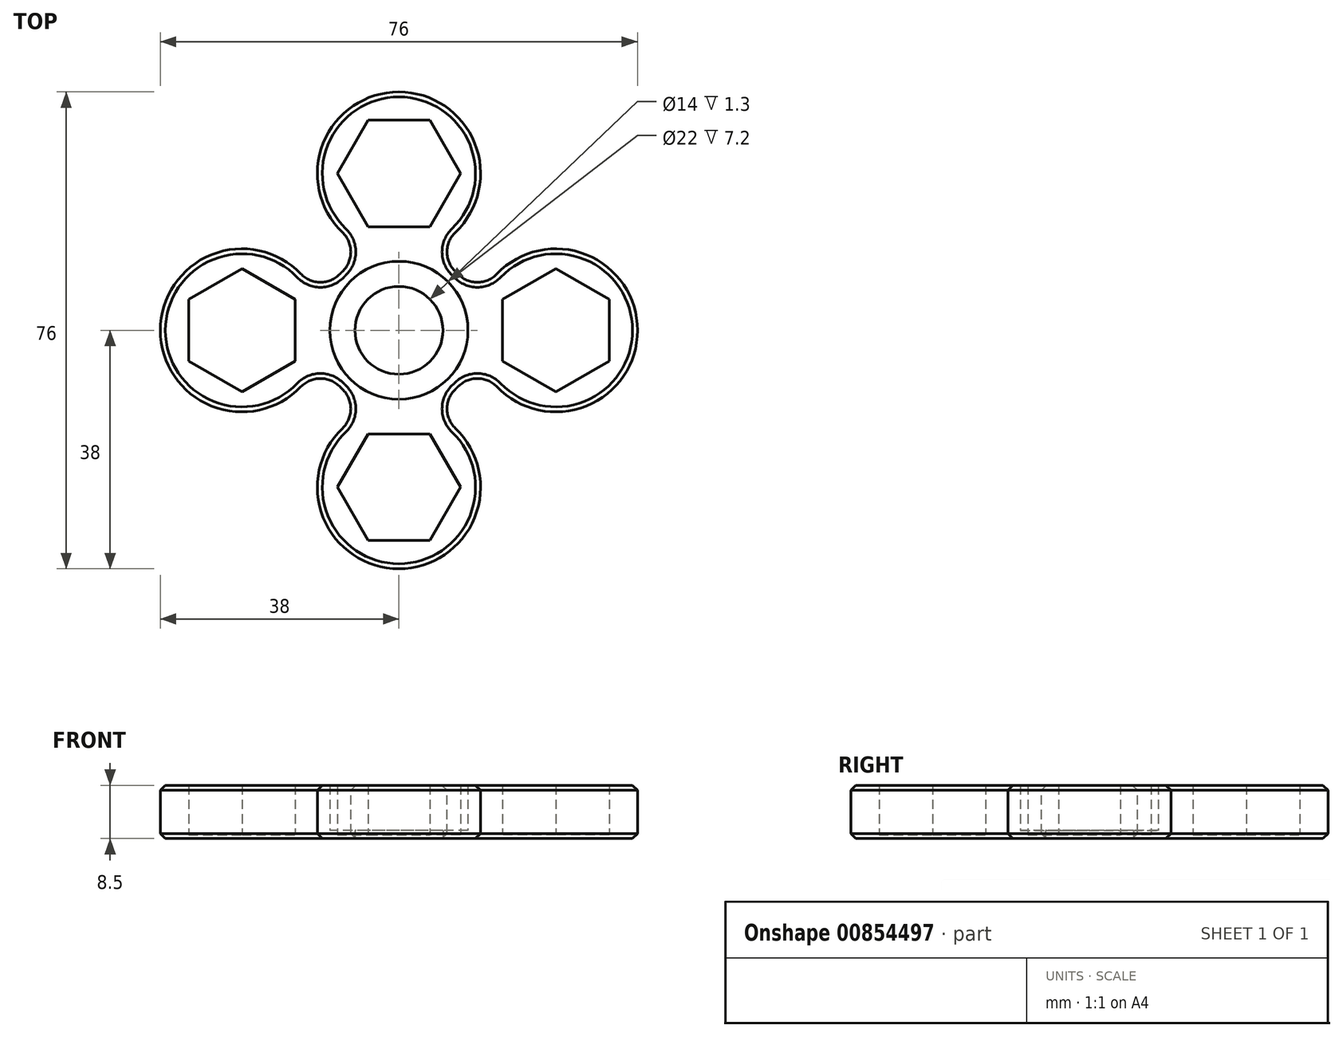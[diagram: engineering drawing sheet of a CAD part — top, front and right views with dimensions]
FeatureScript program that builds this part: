
annotation { "Feature Type Name" : "Feature", "Feature Type Description" : "" }
export const myFeature = defineFeature(function(context is Context, id is Id, definition is map)
    precondition{}
    {
        {
            var Q0;
            Q0=qCreatedBy(makeId("Top.planeOp"),FACE);
            var sketch = newSketch(context, id + "F0", { "sketchPlane" : qUnion([Q0])});
            skCircle(sketch, "E0", {"center": v(0, 0) * mm, "radius": 13 * mm});
            skCircle(sketch, "E1", {"center": v(0, 0) * mm, "radius": 11 * mm});
            skCircle(sketch, "E2", {"center": v(0, 25) * mm, "radius": 13 * mm});
            skCircle(sketch, "E3.cCircle", {"center": v(0, 25) * mm, "radius": 8.5 * mm, "construction": true});
            skLineSegment(sketch, "E3.0", {"start": v(9.81, 25) * mm, "end": v(4.9, 16.5) * mm});
            skLineSegment(sketch, "E3.1", {"start": v(4.9, 16.5) * mm, "end": v(-4.9, 16.5) * mm});
            skLineSegment(sketch, "E3.2", {"start": v(-4.9, 16.5) * mm, "end": v(-9.81, 25) * mm});
            skLineSegment(sketch, "E3.3", {"start": v(-9.81, 25) * mm, "end": v(-4.9, 33.5) * mm});
            skLineSegment(sketch, "E3.4", {"start": v(-4.9, 33.5) * mm, "end": v(4.9, 33.5) * mm});
            skLineSegment(sketch, "E3.5", {"start": v(4.9, 33.5) * mm, "end": v(9.81, 25) * mm});
            skPoint(sketch, "E3.0.midPoint", {"position": v(7.36, 20.75) * mm});
            skCircle(sketch, "E4", {"center": v(0, 0) * mm, "radius": 7 * mm});
            skCircle(sketch, "E5.1.0", {"center": v(-25, 0) * mm, "radius": 13 * mm});
            skLineSegment(sketch, "E5.1.1", {"start": v(-16.5, -4.9) * mm, "end": v(-25, -9.81) * mm});
            skLineSegment(sketch, "E5.1.2", {"start": v(-25, -9.81) * mm, "end": v(-33.5, -4.9) * mm});
            skLineSegment(sketch, "E5.1.3", {"start": v(-33.5, -4.9) * mm, "end": v(-33.5, 4.9) * mm});
            skLineSegment(sketch, "E5.1.4", {"start": v(-33.5, 4.9) * mm, "end": v(-25, 9.81) * mm});
            skLineSegment(sketch, "E5.1.5", {"start": v(-25, 9.81) * mm, "end": v(-16.5, 4.9) * mm});
            skLineSegment(sketch, "E5.1.6", {"start": v(-16.5, 4.9) * mm, "end": v(-16.5, -4.9) * mm});
            skCircle(sketch, "E5.2.0", {"center": v(0, -25) * mm, "radius": 13 * mm});
            skLineSegment(sketch, "E5.2.1", {"start": v(4.9, -16.5) * mm, "end": v(9.81, -25) * mm});
            skLineSegment(sketch, "E5.2.2", {"start": v(9.81, -25) * mm, "end": v(4.9, -33.5) * mm});
            skLineSegment(sketch, "E5.2.3", {"start": v(4.9, -33.5) * mm, "end": v(-4.9, -33.5) * mm});
            skLineSegment(sketch, "E5.2.4", {"start": v(-4.9, -33.5) * mm, "end": v(-9.81, -25) * mm});
            skLineSegment(sketch, "E5.2.5", {"start": v(-9.81, -25) * mm, "end": v(-4.9, -16.5) * mm});
            skLineSegment(sketch, "E5.2.6", {"start": v(-4.9, -16.5) * mm, "end": v(4.9, -16.5) * mm});
            skCircle(sketch, "E5.3.0", {"center": v(25, 0) * mm, "radius": 13 * mm});
            skLineSegment(sketch, "E5.3.1", {"start": v(16.5, 4.9) * mm, "end": v(25, 9.81) * mm});
            skLineSegment(sketch, "E5.3.2", {"start": v(25, 9.81) * mm, "end": v(33.5, 4.9) * mm});
            skLineSegment(sketch, "E5.3.3", {"start": v(33.5, 4.9) * mm, "end": v(33.5, -4.9) * mm});
            skLineSegment(sketch, "E5.3.4", {"start": v(33.5, -4.9) * mm, "end": v(25, -9.81) * mm});
            skLineSegment(sketch, "E5.3.5", {"start": v(25, -9.81) * mm, "end": v(16.5, -4.9) * mm});
            skLineSegment(sketch, "E5.3.6", {"start": v(16.5, -4.9) * mm, "end": v(16.5, 4.9) * mm});
            skSolve(sketch);
        }
        {
            var Q0;
            Q0=makeQuery(id+"F0.imprint","IMPRINT",FACE,{"disambiguationData":[TD([[makeQuery(id+"F0.imprint","IMPRINT",EDGE,{"derivedFrom":sQuery(id+"F0.wireOp",EDGE,"E3.0")}),1.0]])]});
            var Q1;
            Q1=makeQuery(id+"F0.imprint","IMPRINT",FACE,{"disambiguationData":[TD([[makeQuery(id+"F0.imprint","IMPRINT",EDGE,{"derivedFrom":sQuery(id+"F0.wireOp",EDGE,"E3.0")}),-1.0]])]});
            var Q2;
            Q2=makeQuery(id+"F0.imprint","IMPRINT",FACE,{"disambiguationData":[TD([[makeQuery(id+"F0.imprint","IMPRINT",EDGE,{"derivedFrom":sQuery(id+"F0.wireOp",EDGE,"E1")}),1.0]])]});
            var Q3;
            Q3=makeQuery(id+"F0.imprint","IMPRINT",FACE,{"disambiguationData":[TD([[makeQuery(id+"F0.imprint","IMPRINT",EDGE,{"derivedFrom":sQuery(id+"F0.wireOp",EDGE,"E1")}),-1.0]])]});
            var Q4;
            {var subQ0=sQuery(id+"F0.wireOp",EDGE,"E2");var subQ1=sQuery(id+"F0.wireOp",EDGE,"E0");var subQ2=makeQuery(id+"F0.imprint","INTERSECT",VERTEX,{"disambiguationData":[OD(0.0)],"derivedFrom":[subQ1,subQ0]});Q4=makeQuery(id+"F0.imprint","IMPRINT",FACE,{"disambiguationData":[TD([[makeQuery(id+"F0.imprint","IMPRINT",EDGE,{"disambiguationData":[TD([[subQ2,1.0]])],"derivedFrom":subQ1}),1.0]])]});}
            var Q5;
            {var subQ0=sQuery(id+"F0.wireOp",EDGE,"d04d9439-d31e-4a44-955d-4c44843ed1f90.MirrorC");var subQ1=sQuery(id+"F0.wireOp",EDGE,"E0");var subQ2=makeQuery(id+"F0.imprint","INTERSECT",VERTEX,{"disambiguationData":[OD(0.0)],"derivedFrom":[subQ1,subQ0]});Q5=makeQuery(id+"F0.imprint","IMPRINT",FACE,{"disambiguationData":[TD([[makeQuery(id+"F0.imprint","IMPRINT",EDGE,{"disambiguationData":[TD([[subQ2,-1.0]])],"derivedFrom":subQ1}),1.0]])]});}
            var Q6;
            Q6=makeQuery(id+"F0.imprint","IMPRINT",FACE,{"disambiguationData":[TD([[makeQuery(id+"F0.imprint","IMPRINT",EDGE,{"derivedFrom":sQuery(id+"F0.wireOp",EDGE,"235c1c98-600d-46e9-b86c-8ce5ef518ee80.MirrorCS")}),-1.0]])]});
            var Q7;
            Q7=makeQuery(id+"F0.imprint","IMPRINT",FACE,{"disambiguationData":[TD([[makeQuery(id+"F0.imprint","IMPRINT",EDGE,{"derivedFrom":sQuery(id+"F0.wireOp",EDGE,"235c1c98-600d-46e9-b86c-8ce5ef518ee80.MirrorCS")}),1.0]])]});
            var Q8;
            Q8=makeQuery(id+"F0.imprint","IMPRINT",FACE,{"disambiguationData":[TD([[makeQuery(id+"F0.imprint","IMPRINT",EDGE,{"derivedFrom":sQuery(id+"F0.wireOp",EDGE,"E5.1.1")}),1.0]])]});
            var Q9;
            Q9=makeQuery(id+"F0.imprint","IMPRINT",FACE,{"disambiguationData":[TD([[makeQuery(id+"F0.imprint","IMPRINT",EDGE,{"derivedFrom":sQuery(id+"F0.wireOp",EDGE,"E5.1.1")}),-1.0]])]});
            var Q10;
            Q10=makeQuery(id+"F0.imprint","IMPRINT",FACE,{"disambiguationData":[TD([[makeQuery(id+"F0.imprint","IMPRINT",EDGE,{"derivedFrom":sQuery(id+"F0.wireOp",EDGE,"E5.3.1")}),-1.0]])]});
            var Q11;
            Q11=makeQuery(id+"F0.imprint","IMPRINT",FACE,{"disambiguationData":[TD([[makeQuery(id+"F0.imprint","IMPRINT",EDGE,{"derivedFrom":sQuery(id+"F0.wireOp",EDGE,"E5.3.1")}),1.0]])]});
            var Q12;
            Q12=makeQuery(id+"F0.imprint","IMPRINT",FACE,{"disambiguationData":[TD([[makeQuery(id+"F0.imprint","IMPRINT",EDGE,{"derivedFrom":sQuery(id+"F0.wireOp",EDGE,"E5.2.1")}),1.0]])]});
            var Q13;
            Q13=makeQuery(id+"F0.imprint","IMPRINT",FACE,{"disambiguationData":[TD([[makeQuery(id+"F0.imprint","IMPRINT",EDGE,{"derivedFrom":sQuery(id+"F0.wireOp",EDGE,"E5.2.1")}),-1.0]])]});
            var Q14;
            {var subQ0=sQuery(id+"F0.wireOp",EDGE,"E5.2.0");var subQ1=sQuery(id+"F0.wireOp",EDGE,"E0");var subQ2=makeQuery(id+"F0.imprint","INTERSECT",VERTEX,{"disambiguationData":[OD(0.0)],"derivedFrom":[subQ1,subQ0]});Q14=makeQuery(id+"F0.imprint","IMPRINT",FACE,{"disambiguationData":[TD([[makeQuery(id+"F0.imprint","IMPRINT",EDGE,{"disambiguationData":[TD([[subQ2,-1.0]])],"derivedFrom":subQ1}),1.0]])]});}
            var Q15;
            {var subQ0=sQuery(id+"F0.wireOp",EDGE,"E5.3.0");var subQ1=sQuery(id+"F0.wireOp",EDGE,"E0");var subQ2=makeQuery(id+"F0.imprint","INTERSECT",VERTEX,{"disambiguationData":[OD(0.0)],"derivedFrom":[subQ1,subQ0]});Q15=makeQuery(id+"F0.imprint","IMPRINT",FACE,{"disambiguationData":[TD([[makeQuery(id+"F0.imprint","IMPRINT",EDGE,{"disambiguationData":[TD([[subQ2,1.0]])],"derivedFrom":subQ1}),1.0]])]});}
            var Q16;
            {var subQ0=sQuery(id+"F0.wireOp",EDGE,"E5.1.0");var subQ1=sQuery(id+"F0.wireOp",EDGE,"E0");var subQ2=makeQuery(id+"F0.imprint","INTERSECT",VERTEX,{"disambiguationData":[OD(0.0)],"derivedFrom":[subQ1,subQ0]});Q16=makeQuery(id+"F0.imprint","IMPRINT",FACE,{"disambiguationData":[TD([[makeQuery(id+"F0.imprint","IMPRINT",EDGE,{"disambiguationData":[TD([[subQ2,-1.0]])],"derivedFrom":subQ1}),1.0]])]});}
            var Q17;
            {var subQ0=sQuery(id+"F0.wireOp",EDGE,"E2");var subQ1=sQuery(id+"F0.wireOp",EDGE,"E0");var subQ2=makeQuery(id+"F0.imprint","INTERSECT",VERTEX,{"disambiguationData":[OD(0.0)],"derivedFrom":[subQ1,subQ0]});Q17=makeQuery(id+"F0.imprint","IMPRINT",FACE,{"disambiguationData":[TD([[makeQuery(id+"F0.imprint","IMPRINT",EDGE,{"disambiguationData":[TD([[subQ2,-1.0]])],"derivedFrom":subQ1}),1.0]])]});}
            extrude(context, id + "F1", {"entities" : qUnion([Q0, Q1, Q2, Q3, Q4, Q5, Q6, Q7, Q8, Q9, Q10, Q11, Q12, Q13, Q14, Q15, Q16, Q17]), "depth" : 0.6 * mm, "offsetDistance" : 25 * mm});
        }
        {
            var Q0;
            Q0=makeQuery(id+"F0.imprint","IMPRINT",FACE,{"disambiguationData":[TD([[makeQuery(id+"F0.imprint","IMPRINT",EDGE,{"derivedFrom":sQuery(id+"F0.wireOp",EDGE,"E5.3.1")}),1.0]])]});
            var Q1;
            Q1=makeQuery(id+"F0.imprint","IMPRINT",FACE,{"disambiguationData":[TD([[makeQuery(id+"F0.imprint","IMPRINT",EDGE,{"derivedFrom":sQuery(id+"F0.wireOp",EDGE,"E1")}),-1.0]])]});
            var Q2;
            Q2=makeQuery(id+"F0.imprint","IMPRINT",FACE,{"disambiguationData":[TD([[makeQuery(id+"F0.imprint","IMPRINT",EDGE,{"derivedFrom":sQuery(id+"F0.wireOp",EDGE,"E5.2.1")}),1.0]])]});
            var Q3;
            Q3=makeQuery(id+"F0.imprint","IMPRINT",FACE,{"disambiguationData":[TD([[makeQuery(id+"F0.imprint","IMPRINT",EDGE,{"derivedFrom":sQuery(id+"F0.wireOp",EDGE,"E5.1.1")}),1.0]])]});
            var Q4;
            Q4=makeQuery(id+"F0.imprint","IMPRINT",FACE,{"disambiguationData":[TD([[makeQuery(id+"F0.imprint","IMPRINT",EDGE,{"derivedFrom":sQuery(id+"F0.wireOp",EDGE,"E3.0")}),1.0]])]});
            var Q5;
            {var subQ0=sQuery(id+"F0.wireOp",EDGE,"E5.3.0");var subQ1=sQuery(id+"F0.wireOp",EDGE,"E0");var subQ2=makeQuery(id+"F0.imprint","INTERSECT",VERTEX,{"disambiguationData":[OD(0.0)],"derivedFrom":[subQ1,subQ0]});Q5=makeQuery(id+"F0.imprint","IMPRINT",FACE,{"disambiguationData":[TD([[makeQuery(id+"F0.imprint","IMPRINT",EDGE,{"disambiguationData":[TD([[subQ2,1.0]])],"derivedFrom":subQ1}),1.0]])]});}
            var Q6;
            {var subQ0=sQuery(id+"F0.wireOp",EDGE,"E5.2.0");var subQ1=sQuery(id+"F0.wireOp",EDGE,"E0");var subQ2=makeQuery(id+"F0.imprint","INTERSECT",VERTEX,{"disambiguationData":[OD(0.0)],"derivedFrom":[subQ1,subQ0]});Q6=makeQuery(id+"F0.imprint","IMPRINT",FACE,{"disambiguationData":[TD([[makeQuery(id+"F0.imprint","IMPRINT",EDGE,{"disambiguationData":[TD([[subQ2,-1.0]])],"derivedFrom":subQ1}),1.0]])]});}
            var Q7;
            {var subQ0=sQuery(id+"F0.wireOp",EDGE,"E5.1.0");var subQ1=sQuery(id+"F0.wireOp",EDGE,"E0");var subQ2=makeQuery(id+"F0.imprint","INTERSECT",VERTEX,{"disambiguationData":[OD(0.0)],"derivedFrom":[subQ1,subQ0]});Q7=makeQuery(id+"F0.imprint","IMPRINT",FACE,{"disambiguationData":[TD([[makeQuery(id+"F0.imprint","IMPRINT",EDGE,{"disambiguationData":[TD([[subQ2,-1.0]])],"derivedFrom":subQ1}),1.0]])]});}
            var Q8;
            {var subQ0=sQuery(id+"F0.wireOp",EDGE,"E2");var subQ1=sQuery(id+"F0.wireOp",EDGE,"E0");var subQ2=makeQuery(id+"F0.imprint","INTERSECT",VERTEX,{"disambiguationData":[OD(0.0)],"derivedFrom":[subQ1,subQ0]});Q8=makeQuery(id+"F0.imprint","IMPRINT",FACE,{"disambiguationData":[TD([[makeQuery(id+"F0.imprint","IMPRINT",EDGE,{"disambiguationData":[TD([[subQ2,-1.0]])],"derivedFrom":subQ1}),1.0]])]});}
            extrude(context, id + "F2", {"entities" : qUnion([Q0, Q1, Q2, Q3, Q4, Q5, Q6, Q7, Q8]), "operationType" : NewBodyOperationType.ADD, "depth" : 8.5 * mm, "offsetDistance" : 25 * mm});
        }
        {
            var Q0;
            {var subQ0=sQuery(id+"F0.wireOp",EDGE,"d04d9439-d31e-4a44-955d-4c44843ed1f90.MirrorC");var subQ1=sQuery(id+"F0.wireOp",EDGE,"E0");var subQ2=makeQuery(id+"F0.imprint","INTERSECT",VERTEX,{"disambiguationData":[OD(1.0)],"derivedFrom":[subQ1,subQ0]});Q0=makeQuery(id+"F2.boolean.opBoolean","MERGE",EDGE,{"derivedFrom":[makeQuery(id+"F1.opExtrude","SWEPT_EDGE",EDGE,{"disambiguationData":[OSD([subQ1,subQ0]),TDD([subQ2])]}),makeQuery(id+"F2.opExtrude","SWEPT_EDGE",EDGE,{"disambiguationData":[OSD([subQ1,subQ0]),TDD([subQ2])]})]});}
            var Q1;
            {var subQ0=sQuery(id+"F0.wireOp",EDGE,"E2");var subQ1=sQuery(id+"F0.wireOp",EDGE,"E0");var subQ2=makeQuery(id+"F0.imprint","INTERSECT",VERTEX,{"disambiguationData":[OD(1.0)],"derivedFrom":[subQ1,subQ0]});Q1=makeQuery(id+"F2.boolean.opBoolean","MERGE",EDGE,{"derivedFrom":[makeQuery(id+"F1.opExtrude","SWEPT_EDGE",EDGE,{"disambiguationData":[OSD([subQ1,subQ0]),TDD([subQ2])]}),makeQuery(id+"F2.opExtrude","SWEPT_EDGE",EDGE,{"disambiguationData":[OSD([subQ1,subQ0]),TDD([subQ2])]})]});}
            var Q2;
            {var subQ0=sQuery(id+"F0.wireOp",EDGE,"E2");var subQ1=sQuery(id+"F0.wireOp",EDGE,"E0");var subQ2=makeQuery(id+"F0.imprint","INTERSECT",VERTEX,{"disambiguationData":[OD(0.0)],"derivedFrom":[subQ1,subQ0]});Q2=makeQuery(id+"F2.boolean.opBoolean","MERGE",EDGE,{"derivedFrom":[makeQuery(id+"F1.opExtrude","SWEPT_EDGE",EDGE,{"disambiguationData":[OSD([subQ1,subQ0]),TDD([subQ2])]}),makeQuery(id+"F2.opExtrude","SWEPT_EDGE",EDGE,{"disambiguationData":[OSD([subQ1,subQ0]),TDD([subQ2])]})]});}
            var Q3;
            {var subQ0=sQuery(id+"F0.wireOp",EDGE,"d04d9439-d31e-4a44-955d-4c44843ed1f90.MirrorC");var subQ1=sQuery(id+"F0.wireOp",EDGE,"E0");var subQ2=makeQuery(id+"F0.imprint","INTERSECT",VERTEX,{"disambiguationData":[OD(0.0)],"derivedFrom":[subQ1,subQ0]});Q3=makeQuery(id+"F2.boolean.opBoolean","MERGE",EDGE,{"derivedFrom":[makeQuery(id+"F1.opExtrude","SWEPT_EDGE",EDGE,{"disambiguationData":[OSD([subQ1,subQ0]),TDD([subQ2])]}),makeQuery(id+"F2.opExtrude","SWEPT_EDGE",EDGE,{"disambiguationData":[OSD([subQ1,subQ0]),TDD([subQ2])]})]});}
            var Q4;
            {var subQ0=sQuery(id+"F0.wireOp",EDGE,"E5.1.0");var subQ1=sQuery(id+"F0.wireOp",EDGE,"E0");var subQ2=makeQuery(id+"F0.imprint","INTERSECT",VERTEX,{"disambiguationData":[OD(1.0)],"derivedFrom":[subQ1,subQ0]});Q4=makeQuery(id+"F2.boolean.opBoolean","MERGE",EDGE,{"derivedFrom":[makeQuery(id+"F1.opExtrude","SWEPT_EDGE",EDGE,{"disambiguationData":[OSD([subQ1,subQ0]),TDD([subQ2])]}),makeQuery(id+"F2.opExtrude","SWEPT_EDGE",EDGE,{"disambiguationData":[OSD([subQ1,subQ0]),TDD([subQ2])]})]});}
            var Q5;
            {var subQ0=sQuery(id+"F0.wireOp",EDGE,"E5.1.0");var subQ1=sQuery(id+"F0.wireOp",EDGE,"E0");var subQ2=makeQuery(id+"F0.imprint","INTERSECT",VERTEX,{"disambiguationData":[OD(0.0)],"derivedFrom":[subQ1,subQ0]});Q5=makeQuery(id+"F2.boolean.opBoolean","MERGE",EDGE,{"derivedFrom":[makeQuery(id+"F1.opExtrude","SWEPT_EDGE",EDGE,{"disambiguationData":[OSD([subQ1,subQ0]),TDD([subQ2])]}),makeQuery(id+"F2.opExtrude","SWEPT_EDGE",EDGE,{"disambiguationData":[OSD([subQ1,subQ0]),TDD([subQ2])]})]});}
            var Q6;
            {var subQ0=sQuery(id+"F0.wireOp",EDGE,"E5.3.0");var subQ1=sQuery(id+"F0.wireOp",EDGE,"E0");var subQ2=makeQuery(id+"F0.imprint","INTERSECT",VERTEX,{"disambiguationData":[OD(0.0)],"derivedFrom":[subQ1,subQ0]});Q6=makeQuery(id+"F2.boolean.opBoolean","MERGE",EDGE,{"derivedFrom":[makeQuery(id+"F1.opExtrude","SWEPT_EDGE",EDGE,{"disambiguationData":[OSD([subQ1,subQ0]),TDD([subQ2])]}),makeQuery(id+"F2.opExtrude","SWEPT_EDGE",EDGE,{"disambiguationData":[OSD([subQ1,subQ0]),TDD([subQ2])]})]});}
            var Q7;
            {var subQ0=sQuery(id+"F0.wireOp",EDGE,"E5.3.0");var subQ1=sQuery(id+"F0.wireOp",EDGE,"E0");var subQ2=makeQuery(id+"F0.imprint","INTERSECT",VERTEX,{"disambiguationData":[OD(1.0)],"derivedFrom":[subQ1,subQ0]});Q7=makeQuery(id+"F2.boolean.opBoolean","MERGE",EDGE,{"derivedFrom":[makeQuery(id+"F1.opExtrude","SWEPT_EDGE",EDGE,{"disambiguationData":[OSD([subQ1,subQ0]),TDD([subQ2])]}),makeQuery(id+"F2.opExtrude","SWEPT_EDGE",EDGE,{"disambiguationData":[OSD([subQ1,subQ0]),TDD([subQ2])]})]});}
            var Q8;
            {var subQ0=sQuery(id+"F0.wireOp",EDGE,"E5.2.0");var subQ1=sQuery(id+"F0.wireOp",EDGE,"E0");var subQ2=makeQuery(id+"F0.imprint","INTERSECT",VERTEX,{"disambiguationData":[OD(1.0)],"derivedFrom":[subQ1,subQ0]});Q8=makeQuery(id+"F2.boolean.opBoolean","MERGE",EDGE,{"derivedFrom":[makeQuery(id+"F1.opExtrude","SWEPT_EDGE",EDGE,{"disambiguationData":[OSD([subQ1,subQ0]),TDD([subQ2])]}),makeQuery(id+"F2.opExtrude","SWEPT_EDGE",EDGE,{"disambiguationData":[OSD([subQ1,subQ0]),TDD([subQ2])]})]});}
            var Q9;
            {var subQ0=sQuery(id+"F0.wireOp",EDGE,"E5.2.0");var subQ1=sQuery(id+"F0.wireOp",EDGE,"E0");var subQ2=makeQuery(id+"F0.imprint","INTERSECT",VERTEX,{"disambiguationData":[OD(0.0)],"derivedFrom":[subQ1,subQ0]});Q9=makeQuery(id+"F2.boolean.opBoolean","MERGE",EDGE,{"derivedFrom":[makeQuery(id+"F1.opExtrude","SWEPT_EDGE",EDGE,{"disambiguationData":[OSD([subQ1,subQ0]),TDD([subQ2])]}),makeQuery(id+"F2.opExtrude","SWEPT_EDGE",EDGE,{"disambiguationData":[OSD([subQ1,subQ0]),TDD([subQ2])]})]});}
            fillet(context, id + "F3", {"entities" : qUnion([Q0, Q1, Q2, Q3, Q4, Q5, Q6, Q7, Q8, Q9]), "radius" : 4.32 * mm, "tangentPropagation" : true, "allowEdgeOverflow" : false});
        }
        {
            var Q0;
            Q0=makeQuery(id+"F2.opExtrude","CAP_EDGE",EDGE,{"disambiguationData":[OSD([sQuery(id+"F0.wireOp",EDGE,"d04d9439-d31e-4a44-955d-4c44843ed1f90.MirrorC")])],"isStart":false});
            var Q1;
            {var subQ0=sQuery(id+"F0.wireOp",EDGE,"d04d9439-d31e-4a44-955d-4c44843ed1f90.MirrorC");var subQ1=sQuery(id+"F0.wireOp",EDGE,"E0");var subQ2=makeQuery(id+"F0.imprint","INTERSECT",VERTEX,{"disambiguationData":[OD(1.0)],"derivedFrom":[subQ1,subQ0]});Q1=makeQuery(id+"F3.opFillet","BLEND_EDGE",EDGE,{"blendedFrom":[makeQuery(id+"F2.boolean.opBoolean","MERGE",EDGE,{"derivedFrom":[makeQuery(id+"F1.opExtrude","SWEPT_EDGE",EDGE,{"disambiguationData":[OSD([subQ1,subQ0]),TDD([subQ2])]}),makeQuery(id+"F2.opExtrude","SWEPT_EDGE",EDGE,{"disambiguationData":[OSD([subQ1,subQ0]),TDD([subQ2])]})]}),makeQuery(id+"F2.opExtrude","CAP_FACE",FACE,{"disambiguationData":[OSD([subQ1,sQuery(id+"F0.wireOp",EDGE,"E1"),sQuery(id+"F0.wireOp",EDGE,"E2"),sQuery(id+"F0.wireOp",EDGE,"E3.0"),sQuery(id+"F0.wireOp",EDGE,"E3.1"),sQuery(id+"F0.wireOp",EDGE,"E3.2"),sQuery(id+"F0.wireOp",EDGE,"E3.3"),sQuery(id+"F0.wireOp",EDGE,"E3.4"),sQuery(id+"F0.wireOp",EDGE,"E3.5"),subQ0,sQuery(id+"F0.wireOp",EDGE,"235c1c98-600d-46e9-b86c-8ce5ef518ee80.MirrorCS"),sQuery(id+"F0.wireOp",EDGE,"621068df-2c1f-45c7-b7be-a557bf321d120.MirrorCS"),sQuery(id+"F0.wireOp",EDGE,"25bd9b63-27a9-48e3-be2a-9a611c17aff90.MirrorCS"),sQuery(id+"F0.wireOp",EDGE,"6dd50a28-7f5a-452d-aca2-9bb57bd0a7700.MirrorCS"),sQuery(id+"F0.wireOp",EDGE,"15785d12-83de-4acf-9477-1c0fc410dcc50.MirrorCS"),sQuery(id+"F0.wireOp",EDGE,"e7483691-f99c-4309-b820-2ef5816a8e4c0.MirrorCS")])],"isStart":false})],"blendedInto":[makeQuery(id+"F2.opExtrude","CAP_FACE",FACE,{"disambiguationData":[OSD([subQ1,sQuery(id+"F0.wireOp",EDGE,"E1"),sQuery(id+"F0.wireOp",EDGE,"E2"),sQuery(id+"F0.wireOp",EDGE,"E3.0"),sQuery(id+"F0.wireOp",EDGE,"E3.1"),sQuery(id+"F0.wireOp",EDGE,"E3.2"),sQuery(id+"F0.wireOp",EDGE,"E3.3"),sQuery(id+"F0.wireOp",EDGE,"E3.4"),sQuery(id+"F0.wireOp",EDGE,"E3.5"),subQ0,sQuery(id+"F0.wireOp",EDGE,"235c1c98-600d-46e9-b86c-8ce5ef518ee80.MirrorCS"),sQuery(id+"F0.wireOp",EDGE,"621068df-2c1f-45c7-b7be-a557bf321d120.MirrorCS"),sQuery(id+"F0.wireOp",EDGE,"25bd9b63-27a9-48e3-be2a-9a611c17aff90.MirrorCS"),sQuery(id+"F0.wireOp",EDGE,"6dd50a28-7f5a-452d-aca2-9bb57bd0a7700.MirrorCS"),sQuery(id+"F0.wireOp",EDGE,"15785d12-83de-4acf-9477-1c0fc410dcc50.MirrorCS"),sQuery(id+"F0.wireOp",EDGE,"e7483691-f99c-4309-b820-2ef5816a8e4c0.MirrorCS")])],"isStart":false})]});}
            var Q2;
            {var subQ0=sQuery(id+"F0.wireOp",EDGE,"E0");Q2=makeQuery(id+"F2.opExtrude","CAP_EDGE",EDGE,{"disambiguationData":[OSD([subQ0]),TDD([makeQuery(id+"F0.imprint","IMPRINT",EDGE,{"disambiguationData":[TD([[makeQuery(id+"F0.imprint","INTERSECT",VERTEX,{"disambiguationData":[OD(1.0)],"derivedFrom":[subQ0,sQuery(id+"F0.wireOp",EDGE,"E2")]}),1.0]])],"derivedFrom":subQ0})])],"isStart":false});}
            var Q3;
            {var subQ0=sQuery(id+"F0.wireOp",EDGE,"E2");var subQ1=sQuery(id+"F0.wireOp",EDGE,"E0");var subQ2=makeQuery(id+"F0.imprint","INTERSECT",VERTEX,{"disambiguationData":[OD(1.0)],"derivedFrom":[subQ1,subQ0]});Q3=makeQuery(id+"F3.opFillet","BLEND_EDGE",EDGE,{"blendedFrom":[makeQuery(id+"F2.boolean.opBoolean","MERGE",EDGE,{"derivedFrom":[makeQuery(id+"F1.opExtrude","SWEPT_EDGE",EDGE,{"disambiguationData":[OSD([subQ1,subQ0]),TDD([subQ2])]}),makeQuery(id+"F2.opExtrude","SWEPT_EDGE",EDGE,{"disambiguationData":[OSD([subQ1,subQ0]),TDD([subQ2])]})]}),makeQuery(id+"F2.opExtrude","CAP_FACE",FACE,{"disambiguationData":[OSD([subQ1,sQuery(id+"F0.wireOp",EDGE,"E1"),subQ0,sQuery(id+"F0.wireOp",EDGE,"E3.0"),sQuery(id+"F0.wireOp",EDGE,"E3.1"),sQuery(id+"F0.wireOp",EDGE,"E3.2"),sQuery(id+"F0.wireOp",EDGE,"E3.3"),sQuery(id+"F0.wireOp",EDGE,"E3.4"),sQuery(id+"F0.wireOp",EDGE,"E3.5"),sQuery(id+"F0.wireOp",EDGE,"d04d9439-d31e-4a44-955d-4c44843ed1f90.MirrorC"),sQuery(id+"F0.wireOp",EDGE,"235c1c98-600d-46e9-b86c-8ce5ef518ee80.MirrorCS"),sQuery(id+"F0.wireOp",EDGE,"621068df-2c1f-45c7-b7be-a557bf321d120.MirrorCS"),sQuery(id+"F0.wireOp",EDGE,"25bd9b63-27a9-48e3-be2a-9a611c17aff90.MirrorCS"),sQuery(id+"F0.wireOp",EDGE,"6dd50a28-7f5a-452d-aca2-9bb57bd0a7700.MirrorCS"),sQuery(id+"F0.wireOp",EDGE,"15785d12-83de-4acf-9477-1c0fc410dcc50.MirrorCS"),sQuery(id+"F0.wireOp",EDGE,"e7483691-f99c-4309-b820-2ef5816a8e4c0.MirrorCS")])],"isStart":false})],"blendedInto":[makeQuery(id+"F2.opExtrude","CAP_FACE",FACE,{"disambiguationData":[OSD([subQ1,sQuery(id+"F0.wireOp",EDGE,"E1"),subQ0,sQuery(id+"F0.wireOp",EDGE,"E3.0"),sQuery(id+"F0.wireOp",EDGE,"E3.1"),sQuery(id+"F0.wireOp",EDGE,"E3.2"),sQuery(id+"F0.wireOp",EDGE,"E3.3"),sQuery(id+"F0.wireOp",EDGE,"E3.4"),sQuery(id+"F0.wireOp",EDGE,"E3.5"),sQuery(id+"F0.wireOp",EDGE,"d04d9439-d31e-4a44-955d-4c44843ed1f90.MirrorC"),sQuery(id+"F0.wireOp",EDGE,"235c1c98-600d-46e9-b86c-8ce5ef518ee80.MirrorCS"),sQuery(id+"F0.wireOp",EDGE,"621068df-2c1f-45c7-b7be-a557bf321d120.MirrorCS"),sQuery(id+"F0.wireOp",EDGE,"25bd9b63-27a9-48e3-be2a-9a611c17aff90.MirrorCS"),sQuery(id+"F0.wireOp",EDGE,"6dd50a28-7f5a-452d-aca2-9bb57bd0a7700.MirrorCS"),sQuery(id+"F0.wireOp",EDGE,"15785d12-83de-4acf-9477-1c0fc410dcc50.MirrorCS"),sQuery(id+"F0.wireOp",EDGE,"e7483691-f99c-4309-b820-2ef5816a8e4c0.MirrorCS")])],"isStart":false})]});}
            var Q4;
            Q4=makeQuery(id+"F2.opExtrude","CAP_EDGE",EDGE,{"disambiguationData":[OSD([sQuery(id+"F0.wireOp",EDGE,"E2")])],"isStart":false});
            var Q5;
            {var subQ0=sQuery(id+"F0.wireOp",EDGE,"E2");var subQ1=sQuery(id+"F0.wireOp",EDGE,"E0");var subQ2=makeQuery(id+"F0.imprint","INTERSECT",VERTEX,{"disambiguationData":[OD(0.0)],"derivedFrom":[subQ1,subQ0]});Q5=makeQuery(id+"F3.opFillet","BLEND_EDGE",EDGE,{"blendedFrom":[makeQuery(id+"F2.boolean.opBoolean","MERGE",EDGE,{"derivedFrom":[makeQuery(id+"F1.opExtrude","SWEPT_EDGE",EDGE,{"disambiguationData":[OSD([subQ1,subQ0]),TDD([subQ2])]}),makeQuery(id+"F2.opExtrude","SWEPT_EDGE",EDGE,{"disambiguationData":[OSD([subQ1,subQ0]),TDD([subQ2])]})]}),makeQuery(id+"F2.opExtrude","CAP_FACE",FACE,{"disambiguationData":[OSD([subQ1,sQuery(id+"F0.wireOp",EDGE,"E1"),subQ0,sQuery(id+"F0.wireOp",EDGE,"E3.0"),sQuery(id+"F0.wireOp",EDGE,"E3.1"),sQuery(id+"F0.wireOp",EDGE,"E3.2"),sQuery(id+"F0.wireOp",EDGE,"E3.3"),sQuery(id+"F0.wireOp",EDGE,"E3.4"),sQuery(id+"F0.wireOp",EDGE,"E3.5"),sQuery(id+"F0.wireOp",EDGE,"d04d9439-d31e-4a44-955d-4c44843ed1f90.MirrorC"),sQuery(id+"F0.wireOp",EDGE,"235c1c98-600d-46e9-b86c-8ce5ef518ee80.MirrorCS"),sQuery(id+"F0.wireOp",EDGE,"621068df-2c1f-45c7-b7be-a557bf321d120.MirrorCS"),sQuery(id+"F0.wireOp",EDGE,"25bd9b63-27a9-48e3-be2a-9a611c17aff90.MirrorCS"),sQuery(id+"F0.wireOp",EDGE,"6dd50a28-7f5a-452d-aca2-9bb57bd0a7700.MirrorCS"),sQuery(id+"F0.wireOp",EDGE,"15785d12-83de-4acf-9477-1c0fc410dcc50.MirrorCS"),sQuery(id+"F0.wireOp",EDGE,"e7483691-f99c-4309-b820-2ef5816a8e4c0.MirrorCS")])],"isStart":false})],"blendedInto":[makeQuery(id+"F2.opExtrude","CAP_FACE",FACE,{"disambiguationData":[OSD([subQ1,sQuery(id+"F0.wireOp",EDGE,"E1"),subQ0,sQuery(id+"F0.wireOp",EDGE,"E3.0"),sQuery(id+"F0.wireOp",EDGE,"E3.1"),sQuery(id+"F0.wireOp",EDGE,"E3.2"),sQuery(id+"F0.wireOp",EDGE,"E3.3"),sQuery(id+"F0.wireOp",EDGE,"E3.4"),sQuery(id+"F0.wireOp",EDGE,"E3.5"),sQuery(id+"F0.wireOp",EDGE,"d04d9439-d31e-4a44-955d-4c44843ed1f90.MirrorC"),sQuery(id+"F0.wireOp",EDGE,"235c1c98-600d-46e9-b86c-8ce5ef518ee80.MirrorCS"),sQuery(id+"F0.wireOp",EDGE,"621068df-2c1f-45c7-b7be-a557bf321d120.MirrorCS"),sQuery(id+"F0.wireOp",EDGE,"25bd9b63-27a9-48e3-be2a-9a611c17aff90.MirrorCS"),sQuery(id+"F0.wireOp",EDGE,"6dd50a28-7f5a-452d-aca2-9bb57bd0a7700.MirrorCS"),sQuery(id+"F0.wireOp",EDGE,"15785d12-83de-4acf-9477-1c0fc410dcc50.MirrorCS"),sQuery(id+"F0.wireOp",EDGE,"e7483691-f99c-4309-b820-2ef5816a8e4c0.MirrorCS")])],"isStart":false})]});}
            var Q6;
            {var subQ0=sQuery(id+"F0.wireOp",EDGE,"E0");Q6=makeQuery(id+"F2.opExtrude","CAP_EDGE",EDGE,{"disambiguationData":[OSD([subQ0]),TDD([makeQuery(id+"F0.imprint","IMPRINT",EDGE,{"disambiguationData":[TD([[makeQuery(id+"F0.imprint","INTERSECT",VERTEX,{"disambiguationData":[OD(0.0)],"derivedFrom":[subQ0,sQuery(id+"F0.wireOp",EDGE,"E2")]}),-1.0]])],"derivedFrom":subQ0})])],"isStart":false});}
            var Q7;
            {var subQ0=sQuery(id+"F0.wireOp",EDGE,"d04d9439-d31e-4a44-955d-4c44843ed1f90.MirrorC");var subQ1=sQuery(id+"F0.wireOp",EDGE,"E0");var subQ2=makeQuery(id+"F0.imprint","INTERSECT",VERTEX,{"disambiguationData":[OD(0.0)],"derivedFrom":[subQ1,subQ0]});Q7=makeQuery(id+"F3.opFillet","BLEND_EDGE",EDGE,{"blendedFrom":[makeQuery(id+"F2.boolean.opBoolean","MERGE",EDGE,{"derivedFrom":[makeQuery(id+"F1.opExtrude","SWEPT_EDGE",EDGE,{"disambiguationData":[OSD([subQ1,subQ0]),TDD([subQ2])]}),makeQuery(id+"F2.opExtrude","SWEPT_EDGE",EDGE,{"disambiguationData":[OSD([subQ1,subQ0]),TDD([subQ2])]})]}),makeQuery(id+"F2.opExtrude","CAP_FACE",FACE,{"disambiguationData":[OSD([subQ1,sQuery(id+"F0.wireOp",EDGE,"E1"),sQuery(id+"F0.wireOp",EDGE,"E2"),sQuery(id+"F0.wireOp",EDGE,"E3.0"),sQuery(id+"F0.wireOp",EDGE,"E3.1"),sQuery(id+"F0.wireOp",EDGE,"E3.2"),sQuery(id+"F0.wireOp",EDGE,"E3.3"),sQuery(id+"F0.wireOp",EDGE,"E3.4"),sQuery(id+"F0.wireOp",EDGE,"E3.5"),subQ0,sQuery(id+"F0.wireOp",EDGE,"235c1c98-600d-46e9-b86c-8ce5ef518ee80.MirrorCS"),sQuery(id+"F0.wireOp",EDGE,"621068df-2c1f-45c7-b7be-a557bf321d120.MirrorCS"),sQuery(id+"F0.wireOp",EDGE,"25bd9b63-27a9-48e3-be2a-9a611c17aff90.MirrorCS"),sQuery(id+"F0.wireOp",EDGE,"6dd50a28-7f5a-452d-aca2-9bb57bd0a7700.MirrorCS"),sQuery(id+"F0.wireOp",EDGE,"15785d12-83de-4acf-9477-1c0fc410dcc50.MirrorCS"),sQuery(id+"F0.wireOp",EDGE,"e7483691-f99c-4309-b820-2ef5816a8e4c0.MirrorCS")])],"isStart":false})],"blendedInto":[makeQuery(id+"F2.opExtrude","CAP_FACE",FACE,{"disambiguationData":[OSD([subQ1,sQuery(id+"F0.wireOp",EDGE,"E1"),sQuery(id+"F0.wireOp",EDGE,"E2"),sQuery(id+"F0.wireOp",EDGE,"E3.0"),sQuery(id+"F0.wireOp",EDGE,"E3.1"),sQuery(id+"F0.wireOp",EDGE,"E3.2"),sQuery(id+"F0.wireOp",EDGE,"E3.3"),sQuery(id+"F0.wireOp",EDGE,"E3.4"),sQuery(id+"F0.wireOp",EDGE,"E3.5"),subQ0,sQuery(id+"F0.wireOp",EDGE,"235c1c98-600d-46e9-b86c-8ce5ef518ee80.MirrorCS"),sQuery(id+"F0.wireOp",EDGE,"621068df-2c1f-45c7-b7be-a557bf321d120.MirrorCS"),sQuery(id+"F0.wireOp",EDGE,"25bd9b63-27a9-48e3-be2a-9a611c17aff90.MirrorCS"),sQuery(id+"F0.wireOp",EDGE,"6dd50a28-7f5a-452d-aca2-9bb57bd0a7700.MirrorCS"),sQuery(id+"F0.wireOp",EDGE,"15785d12-83de-4acf-9477-1c0fc410dcc50.MirrorCS"),sQuery(id+"F0.wireOp",EDGE,"e7483691-f99c-4309-b820-2ef5816a8e4c0.MirrorCS")])],"isStart":false})]});}
            var Q8;
            Q8=makeQuery(id+"F1.opExtrude","CAP_EDGE",EDGE,{"disambiguationData":[OSD([sQuery(id+"F0.wireOp",EDGE,"d04d9439-d31e-4a44-955d-4c44843ed1f90.MirrorC")])],"isStart":true});
            var Q9;
            {var subQ0=sQuery(id+"F0.wireOp",EDGE,"d04d9439-d31e-4a44-955d-4c44843ed1f90.MirrorC");var subQ1=sQuery(id+"F0.wireOp",EDGE,"E0");var subQ2=makeQuery(id+"F0.imprint","INTERSECT",VERTEX,{"disambiguationData":[OD(0.0)],"derivedFrom":[subQ1,subQ0]});Q9=makeQuery(id+"F3.opFillet","BLEND_EDGE",EDGE,{"blendedFrom":[makeQuery(id+"F2.boolean.opBoolean","MERGE",EDGE,{"derivedFrom":[makeQuery(id+"F1.opExtrude","SWEPT_EDGE",EDGE,{"disambiguationData":[OSD([subQ1,subQ0]),TDD([subQ2])]}),makeQuery(id+"F2.opExtrude","SWEPT_EDGE",EDGE,{"disambiguationData":[OSD([subQ1,subQ0]),TDD([subQ2])]})]}),makeQuery(id+"F1.opExtrude","CAP_FACE",FACE,{"disambiguationData":[OSD([subQ1,sQuery(id+"F0.wireOp",EDGE,"E2"),subQ0,sQuery(id+"F0.wireOp",EDGE,"E4")])],"isStart":true})],"blendedInto":[makeQuery(id+"F1.opExtrude","CAP_FACE",FACE,{"disambiguationData":[OSD([subQ1,sQuery(id+"F0.wireOp",EDGE,"E2"),subQ0,sQuery(id+"F0.wireOp",EDGE,"E4")])],"isStart":true})]});}
            var Q10;
            {var subQ0=sQuery(id+"F0.wireOp",EDGE,"E0");Q10=makeQuery(id+"F1.opExtrude","CAP_EDGE",EDGE,{"disambiguationData":[OSD([subQ0]),TDD([makeQuery(id+"F0.imprint","IMPRINT",EDGE,{"disambiguationData":[TD([[makeQuery(id+"F0.imprint","INTERSECT",VERTEX,{"disambiguationData":[OD(0.0)],"derivedFrom":[subQ0,sQuery(id+"F0.wireOp",EDGE,"E2")]}),-1.0]])],"derivedFrom":subQ0})])],"isStart":true});}
            var Q11;
            {var subQ0=sQuery(id+"F0.wireOp",EDGE,"E2");var subQ1=sQuery(id+"F0.wireOp",EDGE,"E0");var subQ2=makeQuery(id+"F0.imprint","INTERSECT",VERTEX,{"disambiguationData":[OD(0.0)],"derivedFrom":[subQ1,subQ0]});Q11=makeQuery(id+"F3.opFillet","BLEND_EDGE",EDGE,{"blendedFrom":[makeQuery(id+"F2.boolean.opBoolean","MERGE",EDGE,{"derivedFrom":[makeQuery(id+"F1.opExtrude","SWEPT_EDGE",EDGE,{"disambiguationData":[OSD([subQ1,subQ0]),TDD([subQ2])]}),makeQuery(id+"F2.opExtrude","SWEPT_EDGE",EDGE,{"disambiguationData":[OSD([subQ1,subQ0]),TDD([subQ2])]})]}),makeQuery(id+"F1.opExtrude","CAP_FACE",FACE,{"disambiguationData":[OSD([subQ1,subQ0,sQuery(id+"F0.wireOp",EDGE,"d04d9439-d31e-4a44-955d-4c44843ed1f90.MirrorC"),sQuery(id+"F0.wireOp",EDGE,"E4")])],"isStart":true})],"blendedInto":[makeQuery(id+"F1.opExtrude","CAP_FACE",FACE,{"disambiguationData":[OSD([subQ1,subQ0,sQuery(id+"F0.wireOp",EDGE,"d04d9439-d31e-4a44-955d-4c44843ed1f90.MirrorC"),sQuery(id+"F0.wireOp",EDGE,"E4")])],"isStart":true})]});}
            var Q12;
            Q12=makeQuery(id+"F1.opExtrude","CAP_EDGE",EDGE,{"disambiguationData":[OSD([sQuery(id+"F0.wireOp",EDGE,"E2")])],"isStart":true});
            var Q13;
            {var subQ0=sQuery(id+"F0.wireOp",EDGE,"E2");var subQ1=sQuery(id+"F0.wireOp",EDGE,"E0");var subQ2=makeQuery(id+"F0.imprint","INTERSECT",VERTEX,{"disambiguationData":[OD(1.0)],"derivedFrom":[subQ1,subQ0]});Q13=makeQuery(id+"F3.opFillet","BLEND_EDGE",EDGE,{"blendedFrom":[makeQuery(id+"F2.boolean.opBoolean","MERGE",EDGE,{"derivedFrom":[makeQuery(id+"F1.opExtrude","SWEPT_EDGE",EDGE,{"disambiguationData":[OSD([subQ1,subQ0]),TDD([subQ2])]}),makeQuery(id+"F2.opExtrude","SWEPT_EDGE",EDGE,{"disambiguationData":[OSD([subQ1,subQ0]),TDD([subQ2])]})]}),makeQuery(id+"F1.opExtrude","CAP_FACE",FACE,{"disambiguationData":[OSD([subQ1,subQ0,sQuery(id+"F0.wireOp",EDGE,"d04d9439-d31e-4a44-955d-4c44843ed1f90.MirrorC"),sQuery(id+"F0.wireOp",EDGE,"E4")])],"isStart":true})],"blendedInto":[makeQuery(id+"F1.opExtrude","CAP_FACE",FACE,{"disambiguationData":[OSD([subQ1,subQ0,sQuery(id+"F0.wireOp",EDGE,"d04d9439-d31e-4a44-955d-4c44843ed1f90.MirrorC"),sQuery(id+"F0.wireOp",EDGE,"E4")])],"isStart":true})]});}
            var Q14;
            {var subQ0=sQuery(id+"F0.wireOp",EDGE,"E0");Q14=makeQuery(id+"F1.opExtrude","CAP_EDGE",EDGE,{"disambiguationData":[OSD([subQ0]),TDD([makeQuery(id+"F0.imprint","IMPRINT",EDGE,{"disambiguationData":[TD([[makeQuery(id+"F0.imprint","INTERSECT",VERTEX,{"disambiguationData":[OD(1.0)],"derivedFrom":[subQ0,sQuery(id+"F0.wireOp",EDGE,"E2")]}),1.0]])],"derivedFrom":subQ0})])],"isStart":true});}
            var Q15;
            {var subQ0=sQuery(id+"F0.wireOp",EDGE,"d04d9439-d31e-4a44-955d-4c44843ed1f90.MirrorC");var subQ1=sQuery(id+"F0.wireOp",EDGE,"E0");var subQ2=makeQuery(id+"F0.imprint","INTERSECT",VERTEX,{"disambiguationData":[OD(1.0)],"derivedFrom":[subQ1,subQ0]});Q15=makeQuery(id+"F3.opFillet","BLEND_EDGE",EDGE,{"blendedFrom":[makeQuery(id+"F2.boolean.opBoolean","MERGE",EDGE,{"derivedFrom":[makeQuery(id+"F1.opExtrude","SWEPT_EDGE",EDGE,{"disambiguationData":[OSD([subQ1,subQ0]),TDD([subQ2])]}),makeQuery(id+"F2.opExtrude","SWEPT_EDGE",EDGE,{"disambiguationData":[OSD([subQ1,subQ0]),TDD([subQ2])]})]}),makeQuery(id+"F1.opExtrude","CAP_FACE",FACE,{"disambiguationData":[OSD([subQ1,sQuery(id+"F0.wireOp",EDGE,"E2"),subQ0,sQuery(id+"F0.wireOp",EDGE,"E4")])],"isStart":true})],"blendedInto":[makeQuery(id+"F1.opExtrude","CAP_FACE",FACE,{"disambiguationData":[OSD([subQ1,sQuery(id+"F0.wireOp",EDGE,"E2"),subQ0,sQuery(id+"F0.wireOp",EDGE,"E4")])],"isStart":true})]});}
            chamfer(context, id + "F4", {"entities" : qUnion([Q0, Q1, Q2, Q3, Q4, Q5, Q6, Q7, Q8, Q9, Q10, Q11, Q12, Q13, Q14, Q15]), "width" : 0.8 * mm, "tangentPropagation" : true});
        }
        {
            var Q0;
            Q0=makeQuery(id+"F0.imprint","IMPRINT",FACE,{"disambiguationData":[TD([[makeQuery(id+"F0.imprint","IMPRINT",EDGE,{"derivedFrom":sQuery(id+"F0.wireOp",EDGE,"E1")}),1.0]])]});
            extrude(context, id + "F5", {"entities" : qUnion([Q0]), "operationType" : NewBodyOperationType.ADD, "depth" : 1.3 * mm, "offsetDistance" : 25 * mm});
        }
    });
